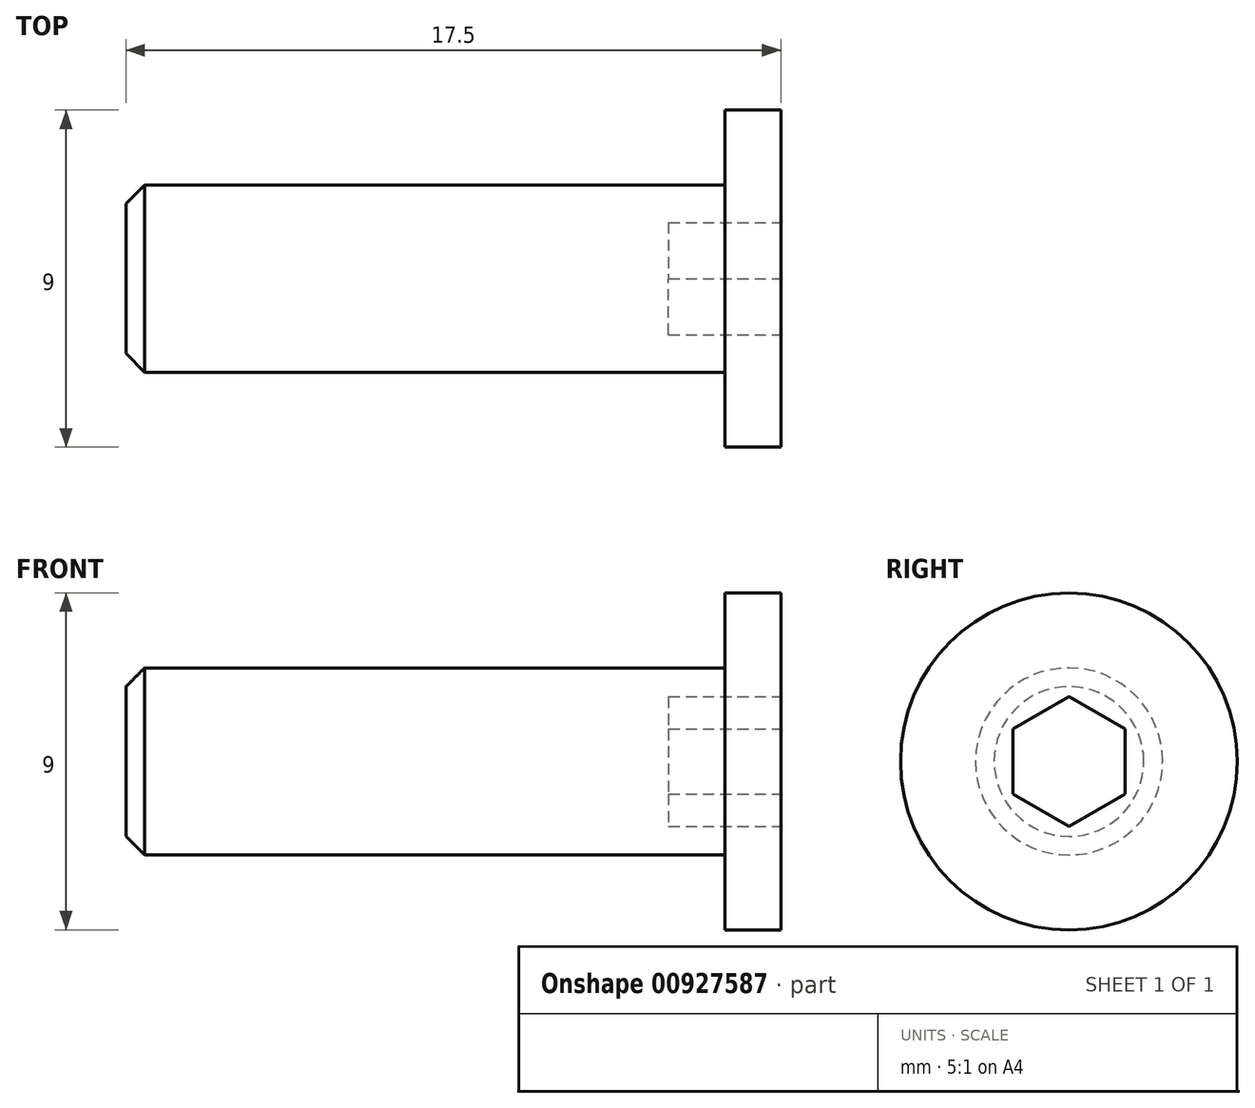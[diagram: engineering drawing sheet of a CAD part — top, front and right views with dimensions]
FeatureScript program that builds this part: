
annotation { "Feature Type Name" : "Feature", "Feature Type Description" : "" }
export const myFeature = defineFeature(function(context is Context, id is Id, definition is map)
    precondition{}
    {
        {
            var Q0;
            Q0=qCreatedBy(makeId("Right.planeOp"),FACE);
            var sketch = newSketch(context, id + "F0", { "sketchPlane" : qUnion([Q0])});
            skCircle(sketch, "E0", {"center": v(0, 0) * mm, "radius": 4.5 * mm});
            skSolve(sketch);
        }
        {
            var Q0;
            Q0 = qSketchRegion(id + "F0", true);
            extrude(context, id + "F1", {"entities" : qUnion([Q0]), "oppositeDirection" : true, "depth" : 1.5 * mm, "offsetDistance" : 25 * mm});
        }
        {
            var Q0;
            Q0=makeQuery(id+"F1.opExtrude","CAP_FACE",FACE,{"disambiguationData":[OSD([sQuery(id+"F0.wireOp",EDGE,"E0")])],"isStart":false});
            var sketch = newSketch(context, id + "F2", { "sketchPlane" : qUnion([Q0])});
            skCircle(sketch, "E1", {"center": v(0, 0) * mm, "radius": 2.5 * mm});
            skSolve(sketch);
        }
        {
            var Q0;
            Q0 = qSketchRegion(id + "F2", true);
            extrude(context, id + "F3", {"entities" : qUnion([Q0]), "operationType" : NewBodyOperationType.ADD, "depth" : 16 * mm, "offsetDistance" : 25 * mm});
        }
        {
            var Q0;
            Q0=makeQuery(id+"F3.opExtrude","CAP_EDGE",EDGE,{"disambiguationData":[OSD([sQuery(id+"F2.wireOp",EDGE,"E1")])],"isStart":false});
            chamfer(context, id + "F4", {"entities" : qUnion([Q0]), "width" : 0.5 * mm, "tangentPropagation" : true});
        }
        {
            var Q0;
            Q0=makeQuery(id+"F1.opExtrude","CAP_FACE",FACE,{"disambiguationData":[OSD([sQuery(id+"F0.wireOp",EDGE,"E0")])],"isStart":true});
            var sketch = newSketch(context, id + "F5", { "sketchPlane" : qUnion([Q0])});
            skLineSegment(sketch, "E2", {"start": v(0, 9.25) * mm, "end": v(0, -9.8) * mm, "construction": true});
            skLineSegment(sketch, "E3", {"start": v(-15.16, 0) * mm, "end": v(15.03, 0) * mm, "construction": true});
            skCircle(sketch, "E4.cCircle", {"center": v(0, 0) * mm, "radius": 1.5 * mm, "construction": true});
            skLineSegment(sketch, "E4.0", {"start": v(1.5, -0.87) * mm, "end": v(0, -1.73) * mm});
            skLineSegment(sketch, "E4.1", {"start": v(0, -1.73) * mm, "end": v(-1.5, -0.87) * mm});
            skLineSegment(sketch, "E4.2", {"start": v(-1.5, -0.87) * mm, "end": v(-1.5, 0.87) * mm});
            skLineSegment(sketch, "E4.3", {"start": v(-1.5, 0.87) * mm, "end": v(0, 1.73) * mm});
            skLineSegment(sketch, "E4.4", {"start": v(0, 1.73) * mm, "end": v(1.5, 0.87) * mm});
            skLineSegment(sketch, "E4.5", {"start": v(1.5, 0.87) * mm, "end": v(1.5, -0.87) * mm});
            skPoint(sketch, "E4.0.midPoint", {"position": v(0.75, -1.3) * mm});
            skSolve(sketch);
        }
        {
            var Q0;
            Q0 = qSketchRegion(id + "F5", true);
            extrude(context, id + "F6", {"entities" : qUnion([Q0]), "operationType" : NewBodyOperationType.REMOVE, "oppositeDirection" : true, "depth" : 3 * mm, "offsetDistance" : 25 * mm});
        }
    });
